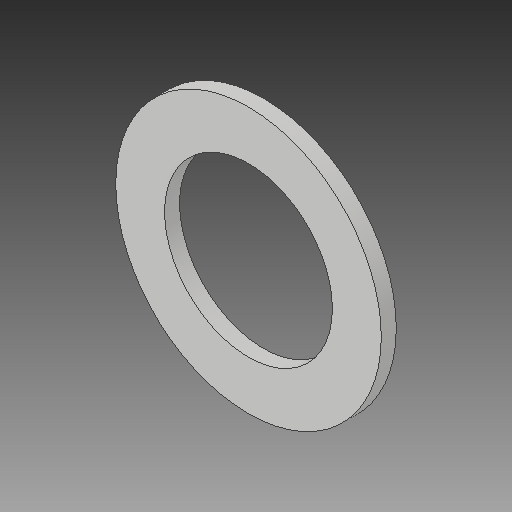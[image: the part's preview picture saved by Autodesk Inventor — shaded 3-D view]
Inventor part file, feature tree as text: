
AUTODESK INVENTOR PART (.ipt)
format: ipt  version: 2018 (Build 220112000, 112)  size: 86,528 bytes
history: native  units: mm
features: extrude x1, sketch x1
ambient origin geometry x8: Origin, YZ Plane, XZ Plane, XY Plane, X Axis, Y Axis, Z Axis, Center Point
bodies: Solid1 (feature_tree)
feature tree (2):
  extrude  "Extrusion1"  [1 undecoded]
  sketch  "Sketch1"  dims[d0=0.7mm d1=0.0mm]
note: 1 required parameter value undecoded (feature->parameter linkage not recoverable at this tier; creation-order binding heuristic only, values carry confidence <= 0.55)
